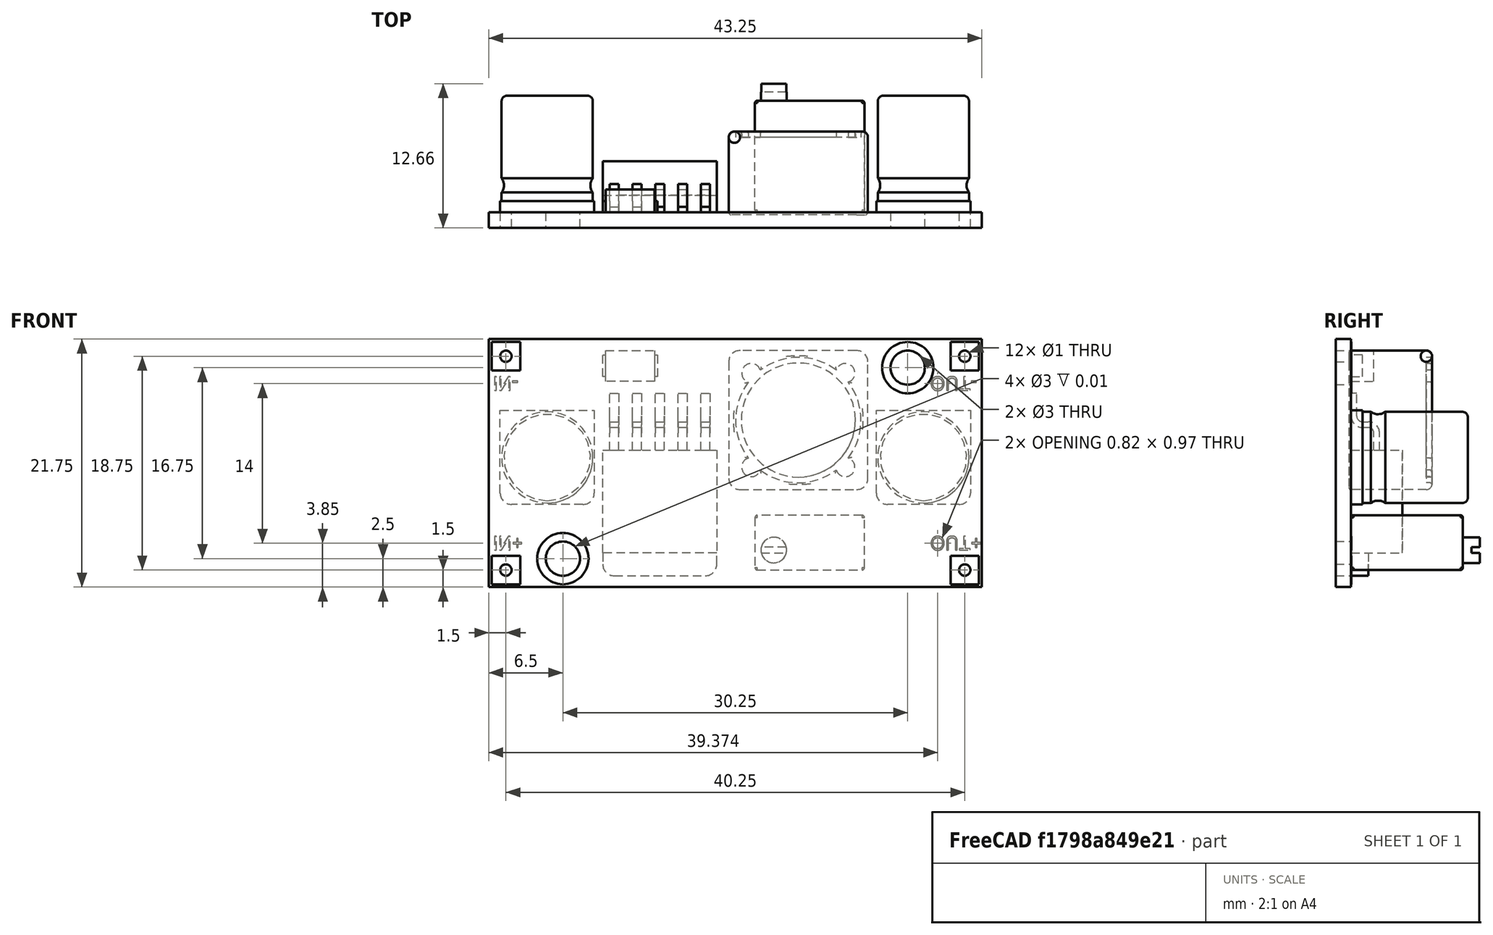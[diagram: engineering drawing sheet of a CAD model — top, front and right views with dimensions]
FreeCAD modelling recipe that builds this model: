
FCSTD DOCUMENT  (FreeCAD 0.19R24267 +148 (Git))
Label: DCDCLM2596_001
License: Public Domain
LicenseURL: http://en.wikipedia.org/wiki/Public_domain
objects: Part::Feature×1, Spreadsheet::Sheet×1, PartDesign::Plane×1, Sketcher::SketchObject×1, PartDesign::Body×1, App::Part×1
note: 4 computed .brp shape members not serialized (recipe doc carries the construction recipe); baked Part::Feature solids carry a one-line shape summary decoded from their .brp

FEATURE [Part::Feature] Feature  label="LM2596DCDC v005"
  shape: bbox 43.27 x 12.68 x 21.77 mm, 474 faces, 44 solids (baked)
FEATURE [Spreadsheet::Sheet] Spreadsheet  label="dcc2596"
  cells = A2=trouDiam; B2(trouDiam)=3; A3=trouDistLong; B3(trouDistLong)=31; A4=trouDistLarg; B4(trouDistLarg)=16.7
FEATURE [PartDesign::Plane] DatumPlane
  AttachmentOffset = pos=(0,0,-3) rot=(0,0,1;0rad)
  Length = 74.5039
  MapMode = 5
  Placement = pos=(0,3,7e-16) rot=(1,0,0;1.5708rad)
  ResizeMode = 0
  Support = -> [XZ_Plane001]
  Width = 61.2478
FEATURE [Sketcher::SketchObject] Sketch
  FullyConstrained = false
  MapMode = 5
  Placement = pos=(0,3,7e-16) rot=(1,0,0;1.5708rad)
  Support = -> [DatumPlane]
  sketch-geometry (2):
    g0: Circle CenterX=36.7561 CenterY=-2.5011 CenterZ=0 NormalX=0 NormalY=0 NormalZ=1 AngleXU=0 Radius=1.5
    g1: Circle CenterX=6.49609 CenterY=-19.2611 CenterZ=0 NormalX=0 NormalY=0 NormalZ=1 AngleXU=0 Radius=1.5
  constraints (4):
    c: Diameter(g1) = 3
    c: Equal(g0,g1)
    c: DistanceX(g1,g0) = 30.26
    c: DistanceY(g1,g0) = 16.76
FEATURE [PartDesign::Body] Body
  Group = -> [DatumPlane,Sketch]
  Origin = -> Origin001
FEATURE [App::Part] Part  label="DCDCLM2596"
  Group = -> [Feature,Spreadsheet,Body]
  Origin = -> Origin
